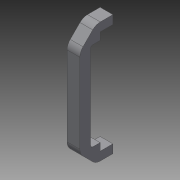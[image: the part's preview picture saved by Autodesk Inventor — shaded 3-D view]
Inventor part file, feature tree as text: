
AUTODESK INVENTOR PART (.ipt)
format: ipt  version: 2016 (Build 200138000, 138)  size: 106,496 bytes
history: native  units: in
note: dims shown in document units (in); Inventor stores cm internally (conversion verified against a paired STEP export)
features: extrude x1, fillet x1, sketch x1
ambient origin geometry x8: Origin, YZ Plane, XZ Plane, XY Plane, X Axis, Y Axis, Z Axis, Center Point
bodies: Solid1 (feature_tree)
feature tree (3):
  extrude  "Extrusion1"  Depth=0.2362in TaperAngle=0.0deg
  fillet  "Fillet1"  Radius=0.3937in
  sketch  "Sketch1"  dims[d4=1.9094in d10=0.2362in d11=0.0in d21=0.3937in d22=0.3937in d31=0.1969in d34=0.1969in d37=0.1575in d46=0.1378in d48=0.0394in d50=0.315in d51=0.1772in d52=0.2362in]
